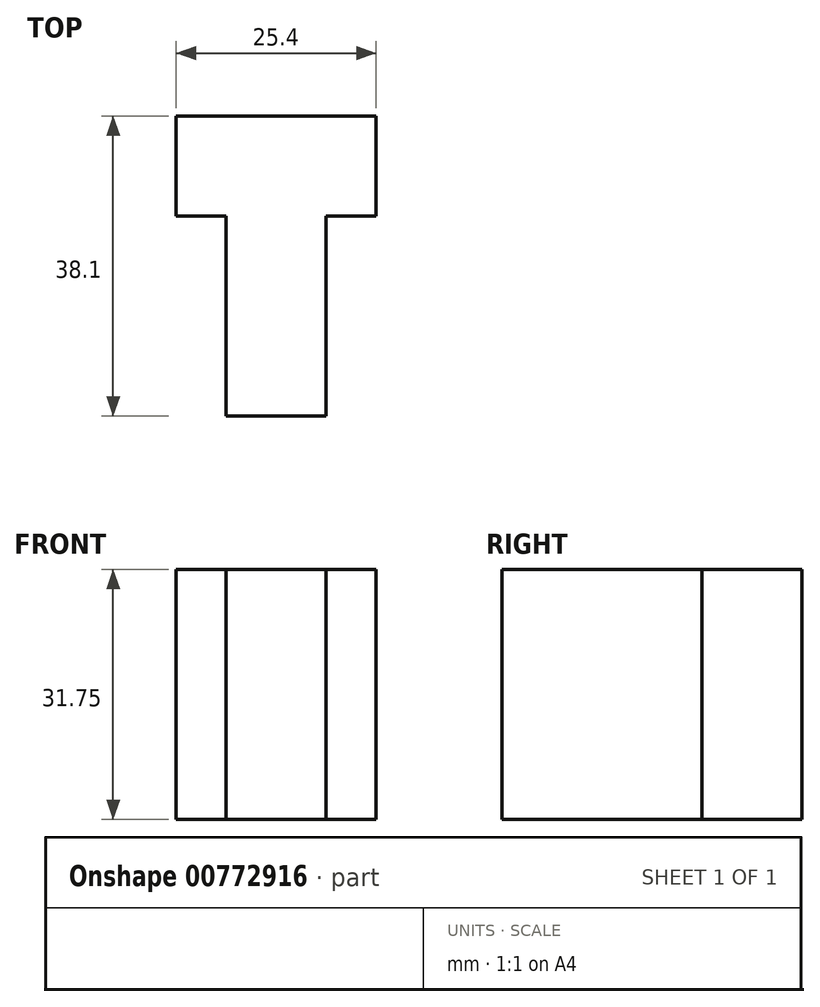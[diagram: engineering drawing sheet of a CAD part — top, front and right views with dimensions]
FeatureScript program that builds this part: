
annotation { "Feature Type Name" : "Feature", "Feature Type Description" : "" }
export const myFeature = defineFeature(function(context is Context, id is Id, definition is map)
    precondition{}
    {
        {
            var Q0;
            Q0=qCreatedBy(makeId("Top.planeOp"),FACE);
            var sketch = newSketch(context, id + "F0", { "sketchPlane" : qUnion([Q0])});
            skLineSegment(sketch, "E0", {"start": v(0, 0) * mm, "end": v(0, -25.4) * mm});
            skLineSegment(sketch, "E1", {"start": v(0, -25.4) * mm, "end": v(12.7, -25.4) * mm});
            skLineSegment(sketch, "E2", {"start": v(12.7, -25.4) * mm, "end": v(12.7, 0) * mm});
            skLineSegment(sketch, "E3", {"start": v(0, 0) * mm, "end": v(-6.35, 0) * mm});
            skLineSegment(sketch, "E4", {"start": v(12.7, 0) * mm, "end": v(19.05, 0) * mm});
            skLineSegment(sketch, "E5", {"start": v(-6.35, 0) * mm, "end": v(-6.35, 12.7) * mm});
            skLineSegment(sketch, "E6", {"start": v(-6.35, 12.7) * mm, "end": v(19.05, 12.7) * mm});
            skLineSegment(sketch, "E7", {"start": v(19.05, 0) * mm, "end": v(19.05, 12.7) * mm});
            skSolve(sketch);
        }
        {
            var Q0;
            Q0=makeQuery(id+"F0.imprint","IMPRINT",FACE,{"disambiguationData":[TD([[makeQuery(id+"F0.imprint","IMPRINT",EDGE,{"derivedFrom":sQuery(id+"F0.wireOp",EDGE,"E0")}),1.0]])]});
            extrude(context, id + "F1", {"entities" : qUnion([Q0]), "depth" : 31.75 * mm, "offsetDistance" : 25.4 * mm});
        }
    });
